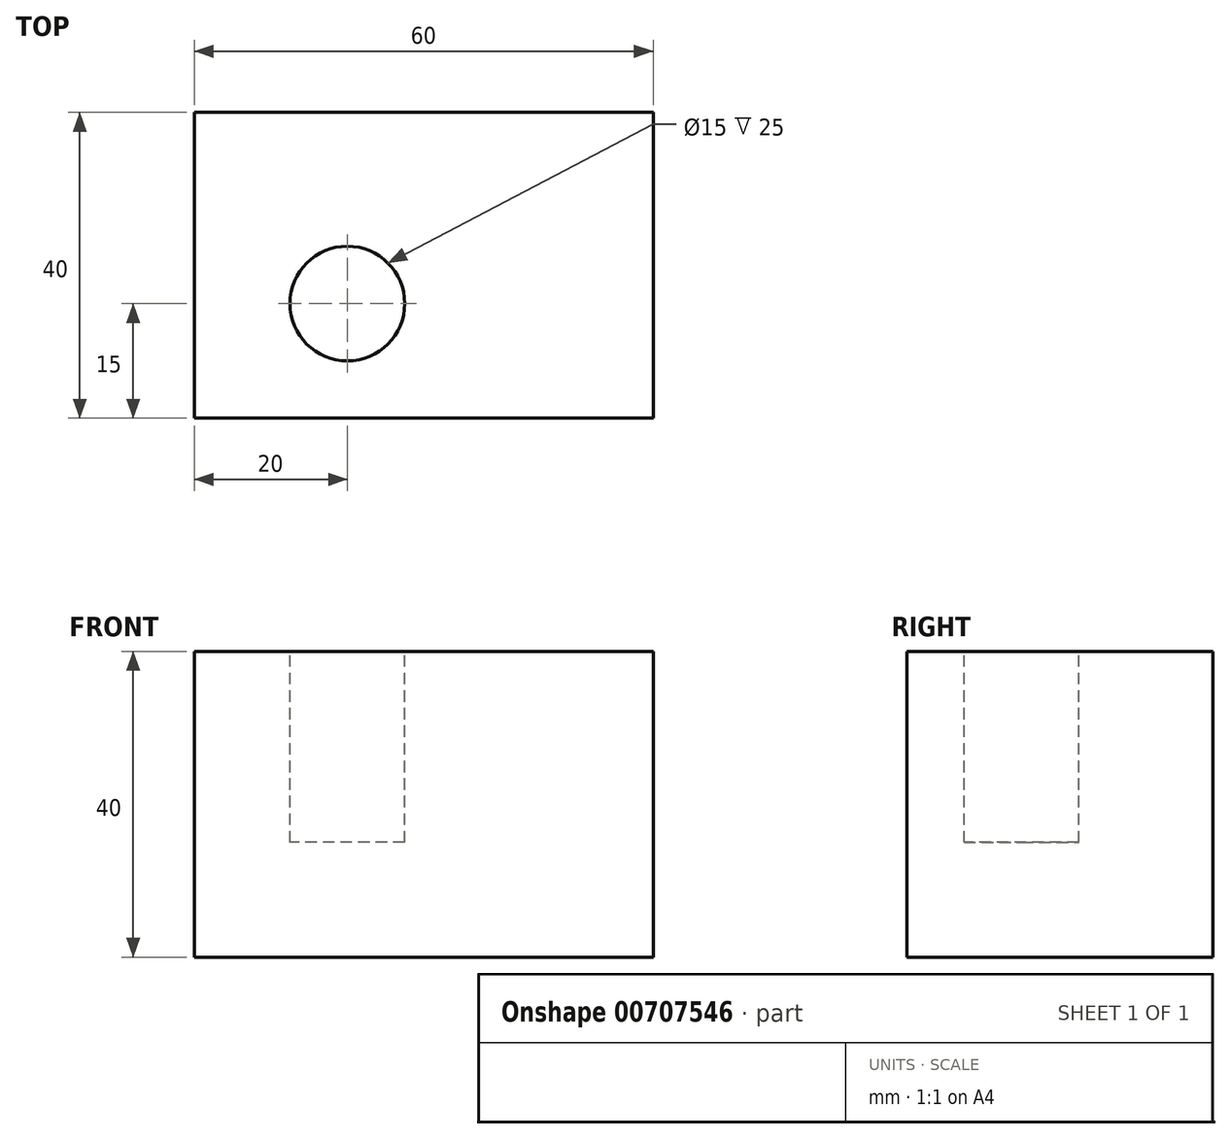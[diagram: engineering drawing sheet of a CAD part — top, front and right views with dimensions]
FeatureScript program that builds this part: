
annotation { "Feature Type Name" : "Feature", "Feature Type Description" : "" }
export const myFeature = defineFeature(function(context is Context, id is Id, definition is map)
    precondition{}
    {
        {
            var Q0;
            Q0=qCreatedBy(makeId("Front.planeOp"),FACE);
            var sketch = newSketch(context, id + "F0", { "sketchPlane" : qUnion([Q0])});
            skLineSegment(sketch, "E0.bottom", {"start": v(0, 0) * mm, "end": v(60, 0) * mm});
            skLineSegment(sketch, "E0.top", {"start": v(0, 40) * mm, "end": v(60, 40) * mm});
            skLineSegment(sketch, "E0.left", {"start": v(0, 0) * mm, "end": v(0, 40) * mm});
            skLineSegment(sketch, "E0.right", {"start": v(60, 0) * mm, "end": v(60, 40) * mm});
            skSolve(sketch);
        }
        {
            var Q0;
            Q0 = qSketchRegion(id + "F0", true);
            extrude(context, id + "F1", {"entities" : qUnion([Q0]), "depth" : 40 * mm, "offsetDistance" : 25 * mm});
        }
        {
            var Q0;
            Q0=makeQuery(id+"F1.opExtrude","SWEPT_FACE",FACE,{"disambiguationData":[OSD([sQuery(id+"F0.wireOp",EDGE,"E0.top")])]});
            var sketch = newSketch(context, id + "F2", { "sketchPlane" : qUnion([Q0])});
            skLineSegment(sketch, "E1.left", {"start": v(0, 0) * mm, "end": v(0, 0) * mm});
            skCircle(sketch, "E2", {"center": v(20, -25) * mm, "radius": 7.5 * mm});
            skSolve(sketch);
        }
        {
            var Q0;
            Q0 = qSketchRegion(id + "F2", true);
            extrude(context, id + "F3", {"entities" : qUnion([Q0]), "operationType" : NewBodyOperationType.REMOVE, "oppositeDirection" : true, "depth" : 25 * mm, "offsetDistance" : 25 * mm});
        }
    });
